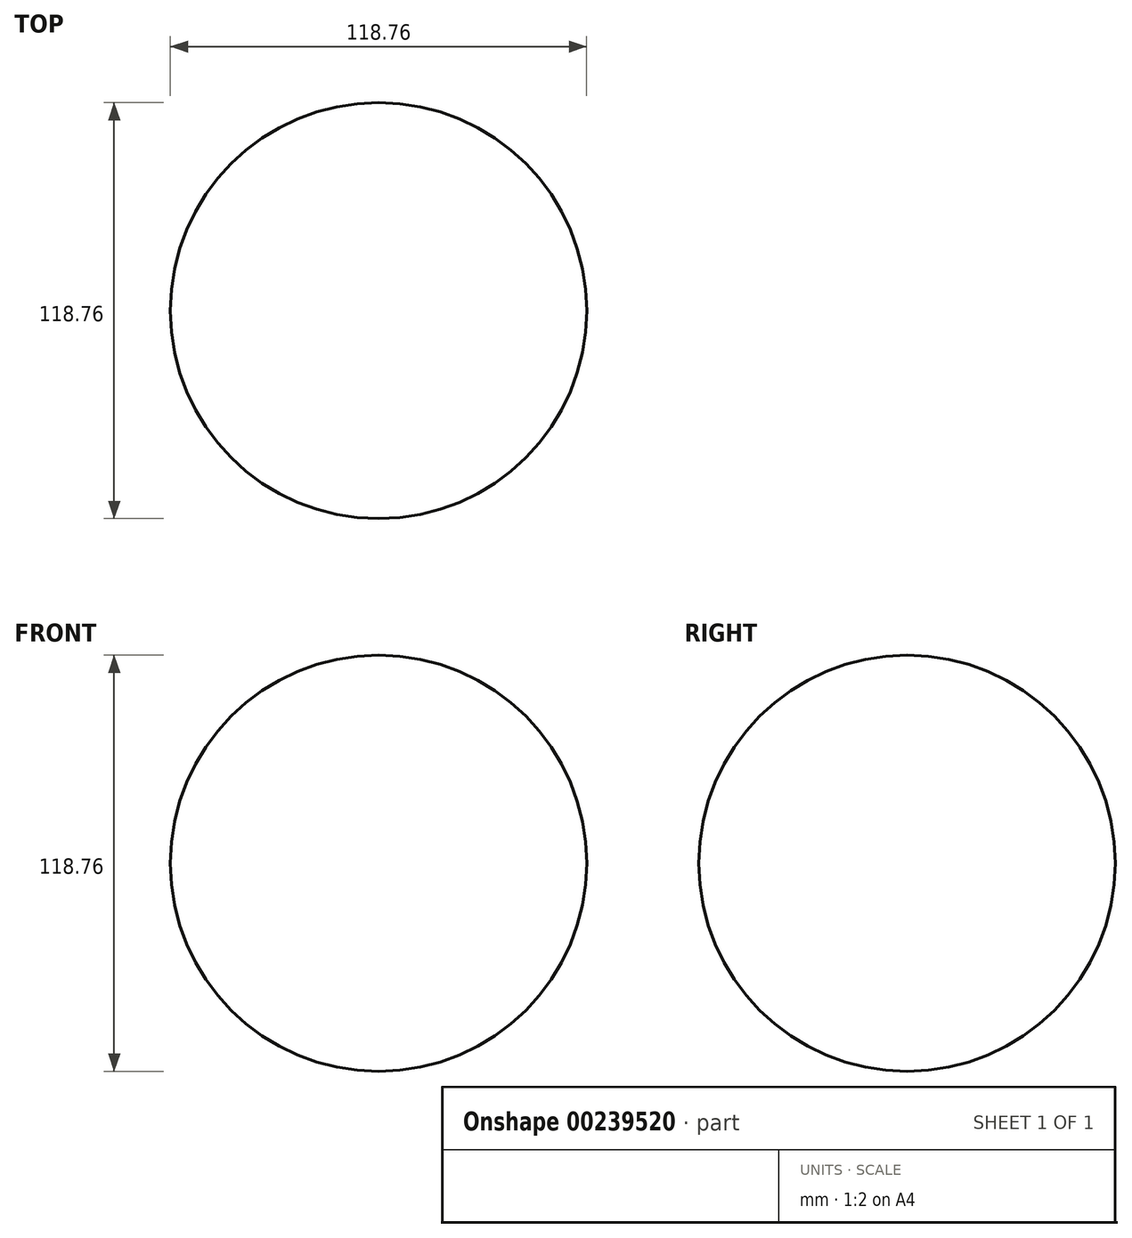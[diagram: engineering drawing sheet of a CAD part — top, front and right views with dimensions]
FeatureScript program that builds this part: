
annotation { "Feature Type Name" : "Feature", "Feature Type Description" : "" }
export const myFeature = defineFeature(function(context is Context, id is Id, definition is map)
    precondition{}
    {
        {
            var Q0;
            Q0=qCreatedBy(makeId("Front.planeOp"),FACE);
            var sketch = newSketch(context, id + "F0", { "sketchPlane" : qUnion([Q0])});
            skArc(sketch, "E0", {"start": v(0, -59.38) * mm, "mid": v(59.38, 0) * mm, "end": v(0, 59.38) * mm});
            skLineSegment(sketch, "E1", {"start": v(0, 59.38) * mm, "end": v(0, -59.38) * mm});
            skSolve(sketch);
        }
        {
            var Q0;
            Q0 = qSketchRegion(id + "F0", true);
            var Q1;
            Q1=sQuery(id+"F0.wireOp",EDGE,"E1");
            revolve(context, id + "F1", {"entities" : qUnion([Q0]), "axis" : qUnion([Q1]), "revolveType" : RevolveType.FULL});
        }
    });
